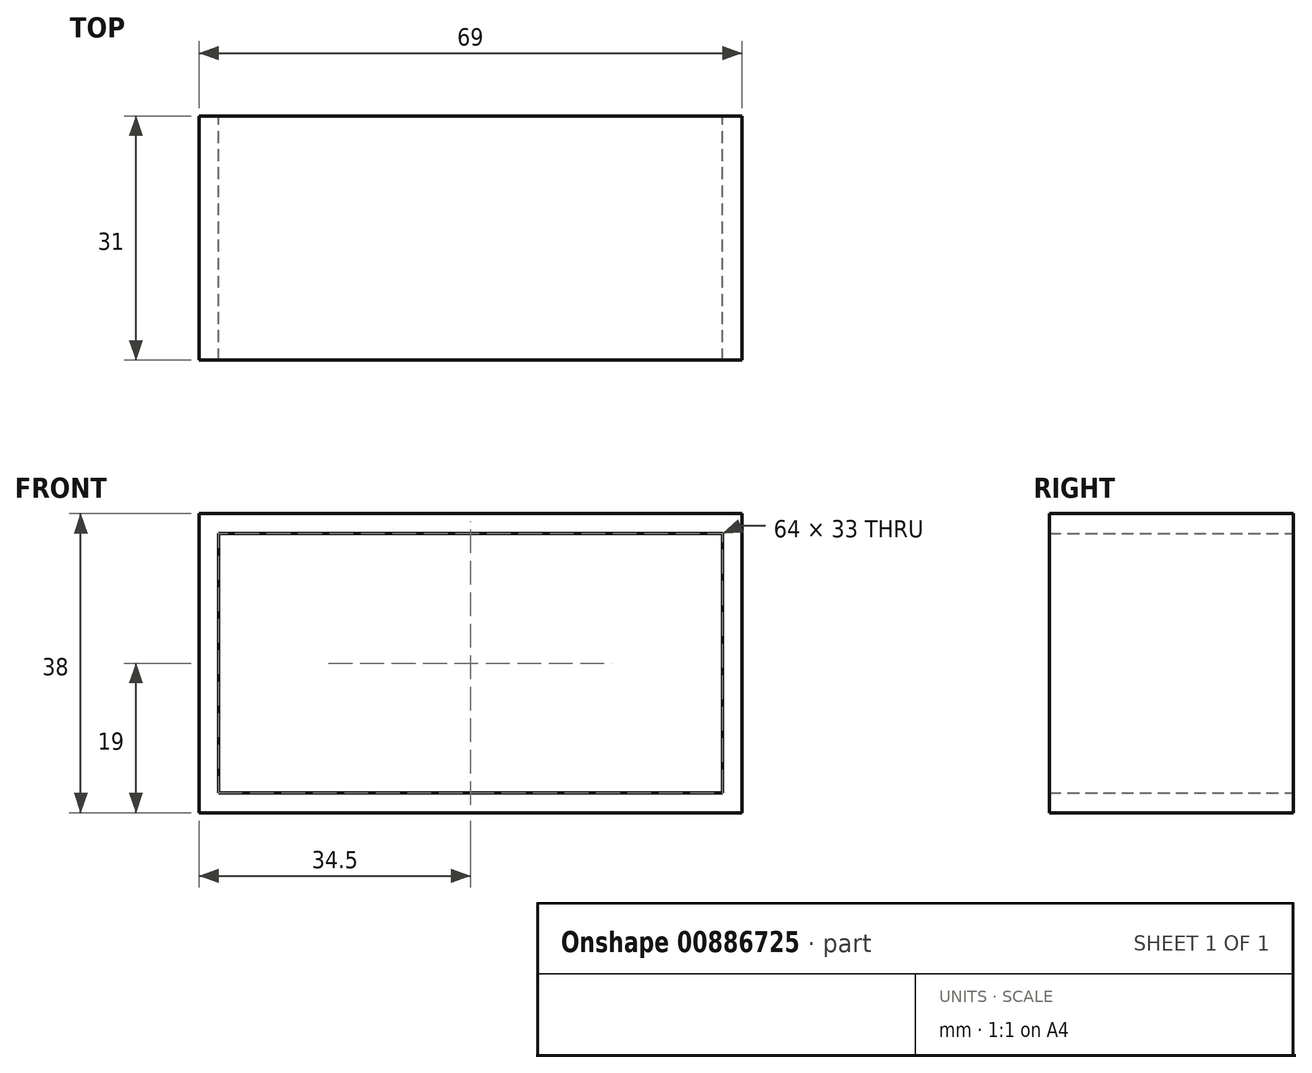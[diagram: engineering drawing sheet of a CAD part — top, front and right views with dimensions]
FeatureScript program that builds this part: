
annotation { "Feature Type Name" : "Feature", "Feature Type Description" : "" }
export const myFeature = defineFeature(function(context is Context, id is Id, definition is map)
    precondition{}
    {
        {
            var Q0;
            Q0=qCreatedBy(makeId("Front.planeOp"),FACE);
            var sketch = newSketch(context, id + "F0", { "sketchPlane" : qUnion([Q0])});
            skLineSegment(sketch, "E0.bottom", {"start": v(-32, 16.5) * mm, "end": v(32, 16.5) * mm});
            skLineSegment(sketch, "E0.top", {"start": v(-32, -16.5) * mm, "end": v(32, -16.5) * mm});
            skLineSegment(sketch, "E0.left", {"start": v(-32, 16.5) * mm, "end": v(-32, -16.5) * mm});
            skLineSegment(sketch, "E0.right", {"start": v(32, 16.5) * mm, "end": v(32, -16.5) * mm});
            skPoint(sketch, "E0.middle", {"position": v(0, 0) * mm});
            skLineSegment(sketch, "E1.0", {"start": v(-34.5, 19) * mm, "end": v(34.5, 19) * mm});
            skLineSegment(sketch, "E1.1", {"start": v(-34.5, 19) * mm, "end": v(-34.5, -19) * mm});
            skLineSegment(sketch, "E1.2", {"start": v(-34.5, -19) * mm, "end": v(34.5, -19) * mm});
            skLineSegment(sketch, "E1.3", {"start": v(34.5, 19) * mm, "end": v(34.5, -19) * mm});
            skSolve(sketch);
        }
        {
            var Q0;
            Q0=makeQuery(id+"F0.imprint","IMPRINT",FACE,{"disambiguationData":[TD([[makeQuery(id+"F0.imprint","IMPRINT",EDGE,{"derivedFrom":sQuery(id+"F0.wireOp",EDGE,"E0.bottom")}),1.0]])]});
            extrude(context, id + "F1", {"entities" : qUnion([Q0]), "depth" : 31 * mm, "offsetDistance" : 25 * mm});
        }
    });
